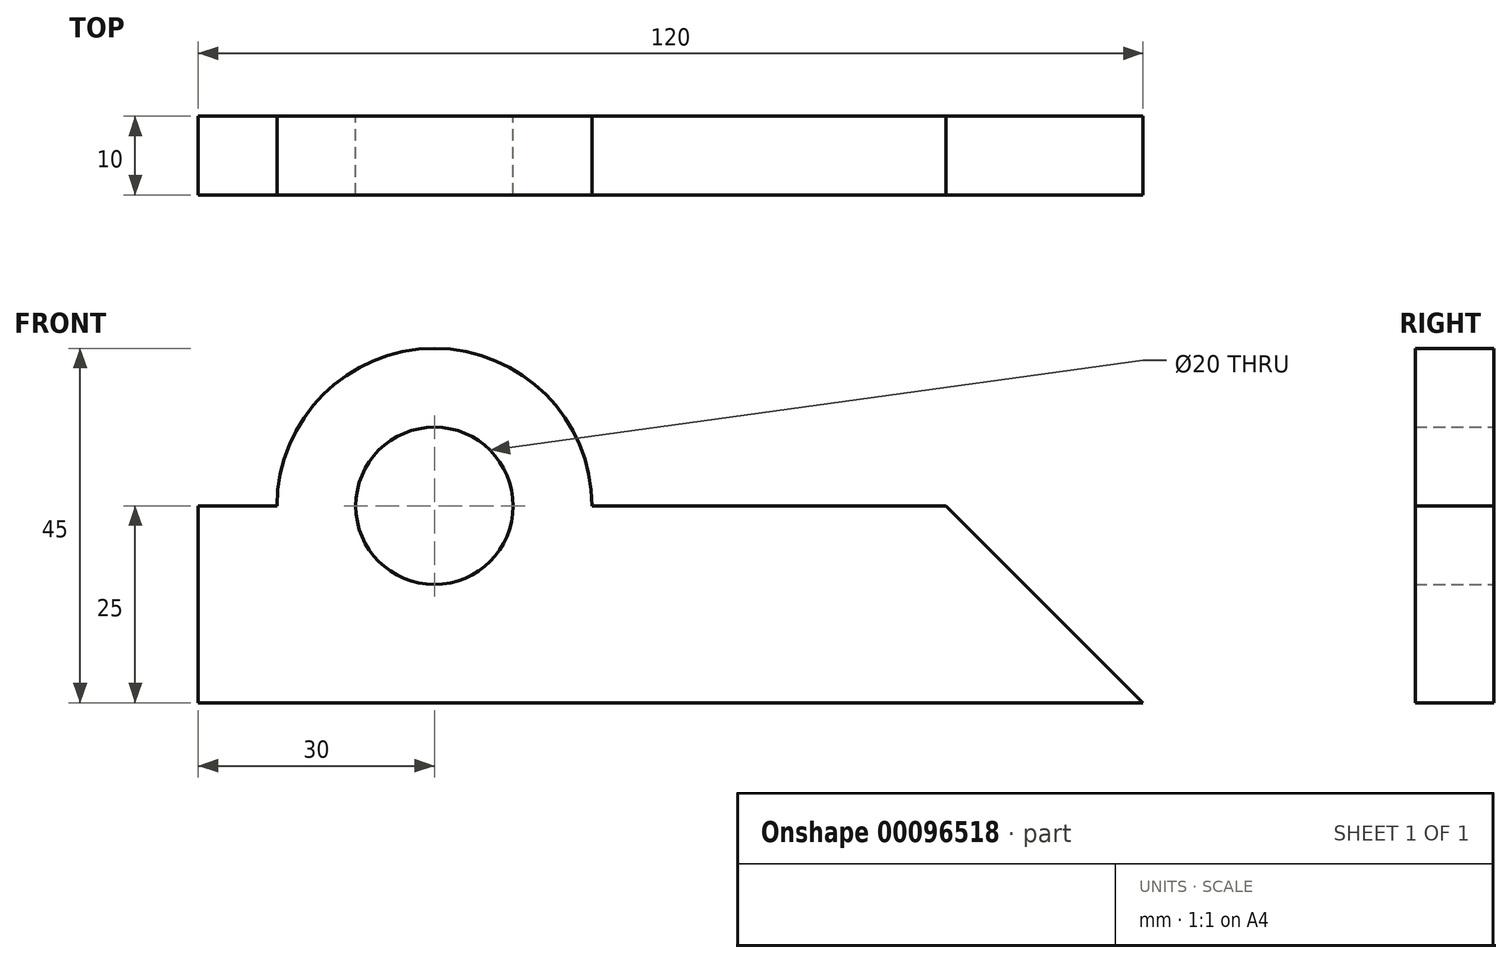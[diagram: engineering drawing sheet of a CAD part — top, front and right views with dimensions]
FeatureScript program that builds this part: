
annotation { "Feature Type Name" : "Feature", "Feature Type Description" : "" }
export const myFeature = defineFeature(function(context is Context, id is Id, definition is map)
    precondition{}
    {
        {
            var Q0;
            Q0=qCreatedBy(makeId("Front.planeOp"),FACE);
            var sketch = newSketch(context, id + "F0", { "sketchPlane" : qUnion([Q0])});
            skLineSegment(sketch, "E0", {"start": v(0, 0) * mm, "end": v(0, 25) * mm});
            skLineSegment(sketch, "E1", {"start": v(0, 0) * mm, "end": v(120, 0) * mm});
            skLineSegment(sketch, "E2", {"start": v(120, 0) * mm, "end": v(95, 25) * mm});
            skLineSegment(sketch, "E3", {"start": v(0, 25) * mm, "end": v(10, 25) * mm});
            skArc(sketch, "E4", {"start": v(50, 25) * mm, "mid": v(30, 45) * mm, "end": v(10, 25) * mm});
            skCircle(sketch, "E5", {"center": v(30, 25) * mm, "radius": 10 * mm});
            skLineSegment(sketch, "E6", {"start": v(95, 25) * mm, "end": v(50, 25) * mm});
            skSolve(sketch);
        }
        {
            var Q0;
            Q0 = qSketchRegion(id + "F0", true);
            extrude(context, id + "F1", {"entities" : qUnion([Q0]), "depth" : 10 * mm});
        }
    });
